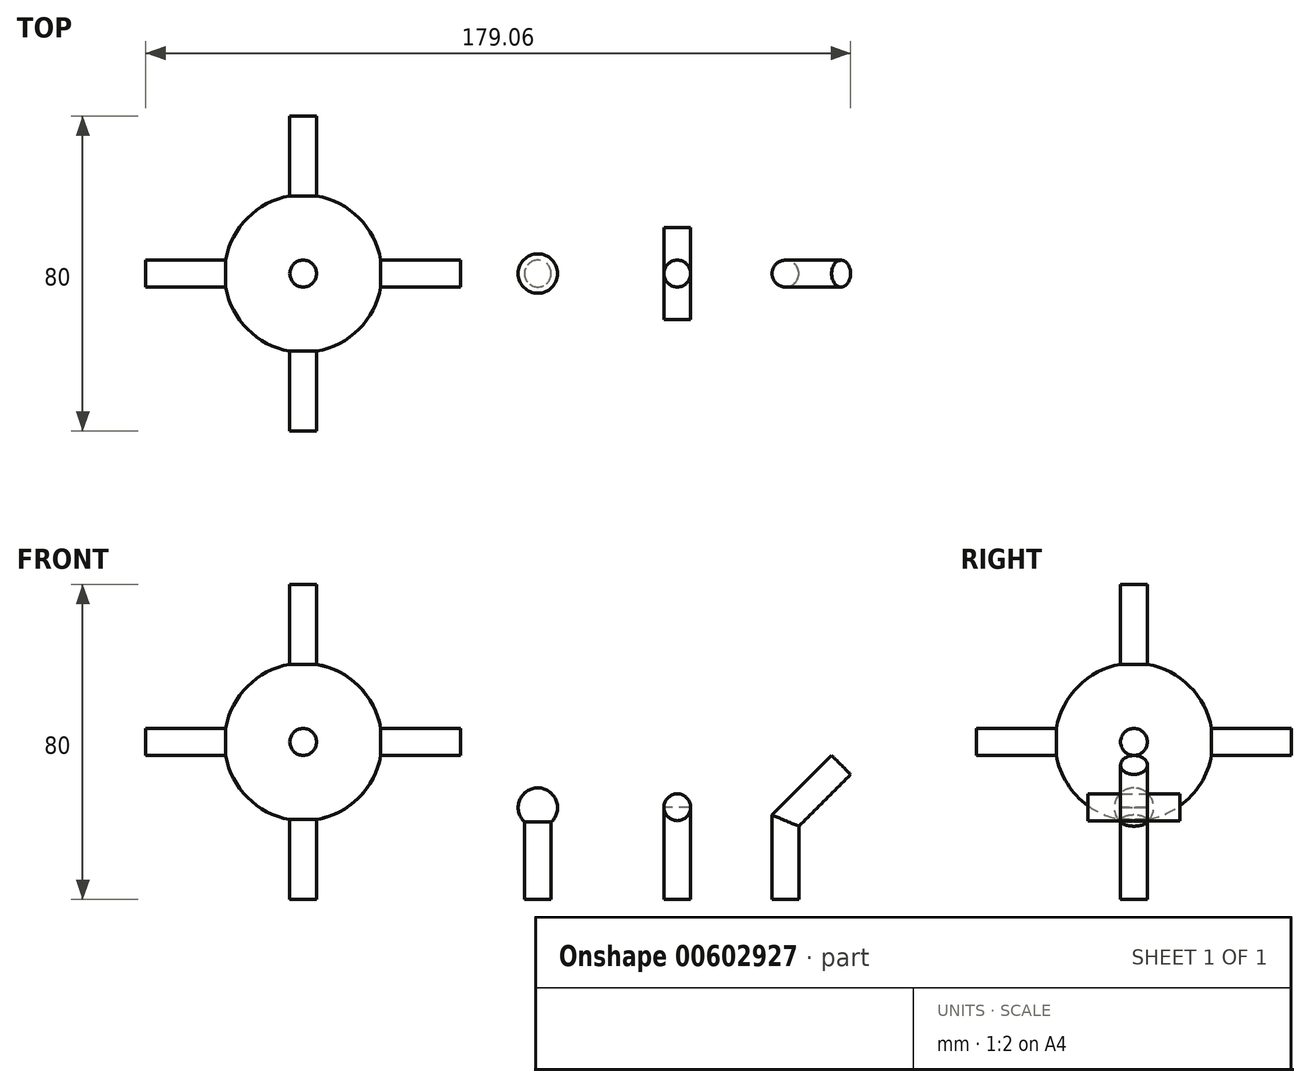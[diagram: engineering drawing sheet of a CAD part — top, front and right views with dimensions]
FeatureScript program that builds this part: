
annotation { "Feature Type Name" : "Feature", "Feature Type Description" : "" }
export const myFeature = defineFeature(function(context is Context, id is Id, definition is map)
    precondition{}
    {
        {
            var Q0;
            Q0=qCreatedBy(makeId("Top.planeOp"),FACE);
            var sketch = newSketch(context, id + "F0", { "sketchPlane" : qUnion([Q0])});
            skCircle(sketch, "E0", {"center": v(0, 0) * mm, "radius": 3.4 * mm});
            skSolve(sketch);
        }
        {
            var Q0;
            Q0 = qSketchRegion(id + "F0", true);
            extrude(context, id + "F1", {"entities" : qUnion([Q0]), "depth" : 20 * mm, "offsetDistance" : 25.4 * mm});
        }
        {
            var Q0;
            Q0=qCreatedBy(makeId("Right.planeOp"),FACE);
            var sketch = newSketch(context, id + "F2", { "sketchPlane" : qUnion([Q0])});
            skLineSegment(sketch, "E1", {"start": v(0, 18.32) * mm, "end": v(0, 28.32) * mm});
            skArc(sketch, "E2", {"start": v(0, 18.32) * mm, "mid": v(5, 23.32) * mm, "end": v(0, 28.32) * mm});
            skSolve(sketch);
        }
        {
            var Q0;
            Q0 = qSketchRegion(id + "F2", true);
            var Q1;
            Q1=makeQuery(id+"F1.opExtrude","SWEPT_FACE",FACE,{"disambiguationData":[OSD([sQuery(id+"F0.wireOp",EDGE,"E0")])]});
            revolve(context, id + "F3", {"operationType" : NewBodyOperationType.ADD, "entities" : qUnion([Q0]), "axis" : qUnion([Q1]), "revolveType" : RevolveType.FULL});
        }
        {
            var Q0;
            Q0=qCreatedBy(makeId("Top.planeOp"),FACE);
            var sketch = newSketch(context, id + "F4", { "sketchPlane" : qUnion([Q0])});
            skCircle(sketch, "E3", {"center": v(35.42, 0) * mm, "radius": 3.4 * mm});
            skSolve(sketch);
        }
        {
            var Q0;
            Q0 = qSketchRegion(id + "F4", true);
            extrude(context, id + "F5", {"entities" : qUnion([Q0]), "depth" : 23.4 * mm, "offsetDistance" : 25 * mm});
        }
        {
            var Q0;
            Q0=qCreatedBy(makeId("Front.planeOp"),FACE);
            var sketch = newSketch(context, id + "F6", { "sketchPlane" : qUnion([Q0])});
            skCircle(sketch, "E4", {"center": v(35.42, 23.4) * mm, "radius": 3.4 * mm});
            skLineSegment(sketch, "E5.0", {"start": v(32.02, 23.4) * mm, "end": v(38.82, 23.4) * mm, "construction": true});
            skSolve(sketch);
        }
        {
            var Q0;
            Q0=makeQuery(id+"F6.imprint","IMPRINT",FACE,{"disambiguationData":[TD([[makeQuery(id+"F6.imprint","IMPRINT",EDGE,{"derivedFrom":sQuery(id+"F6.wireOp",EDGE,"E4")}),1.0]])]});
            var Q1;
            Q1 = qConstructionFilter(qBodyType(qCreatedBy(id + "F6" ,EDGE), BodyType.WIRE), ConstructionObject.NO);
            extrude(context, id + "F7", {"entities" : qUnion([Q0]), "surfaceEntities" : qUnion([Q1]), "endBound" : BoundingType.SYMMETRIC, "depth" : (46.8 / 2) * mm, "offsetDistance" : 25 * mm});
        }
        {
            var Q0;
            Q0=qCreatedBy(makeId("Front.planeOp"),FACE);
            var sketch = newSketch(context, id + "F8", { "sketchPlane" : qUnion([Q0])});
            skLineSegment(sketch, "E6", {"start": v(62.9, 0) * mm, "end": v(62.9, 20) * mm});
            skLineSegment(sketch, "E7", {"start": v(62.9, 20) * mm, "end": v(77.04, 34.14) * mm});
            skSolve(sketch);
        }
        {
            var Q0;
            Q0=qCreatedBy(makeId("Top.planeOp"),FACE);
            var sketch = newSketch(context, id + "F9", { "sketchPlane" : qUnion([Q0])});
            skPoint(sketch, "E8.0", {"position": v(62.9, 0) * mm});
            skCircle(sketch, "E9", {"center": v(62.9, 0) * mm, "radius": 3.4 * mm});
            skSolve(sketch);
        }
        {
            var Q0;
            Q0=makeQuery(id+"F9.imprint","IMPRINT",FACE,{"disambiguationData":[TD([[makeQuery(id+"F9.imprint","IMPRINT",EDGE,{"derivedFrom":sQuery(id+"F9.wireOp",EDGE,"E9")}),1.0]])]});
            var Q1;
            Q1=sQuery(id+"F8.wireOp",EDGE,"E6");
            var Q2;
            Q2=sQuery(id+"F8.wireOp",EDGE,"E7");
            sweep(context, id + "F10", {"profiles" : qUnion([Q0]), "path" : qUnion([Q1, Q2])});
        }
        {
            var Q0;
            Q0=qCreatedBy(makeId("Top.planeOp"),FACE);
            var sketch = newSketch(context, id + "F11", { "sketchPlane" : qUnion([Q0])});
            skCircle(sketch, "E10", {"center": v(-59.62, 0) * mm, "radius": 3.4 * mm});
            skSolve(sketch);
        }
        {
            var Q0;
            Q0 = qSketchRegion(id + "F11", true);
            extrude(context, id + "F12", {"entities" : qUnion([Q0]), "depth" : 80 * mm, "offsetDistance" : 25 * mm});
        }
        {
            var Q0;
            Q0=qCreatedBy(makeId("Front.planeOp"),FACE);
            var sketch = newSketch(context, id + "F13", { "sketchPlane" : qUnion([Q0])});
            skLineSegment(sketch, "E11.0", {"start": v(-63.02, 0) * mm, "end": v(-56.22, 0) * mm, "construction": true});
            skCircle(sketch, "E12", {"center": v(-59.62, 40) * mm, "radius": 3.4 * mm});
            skPoint(sketch, "E12.centerSnap0", {"position": v(-59.62, 0) * mm});
            skSolve(sketch);
        }
        {
            var Q0;
            Q0 = qSketchRegion(id + "F13", true);
            extrude(context, id + "F14", {"entities" : qUnion([Q0]), "operationType" : NewBodyOperationType.ADD, "endBound" : BoundingType.SYMMETRIC, "depth" : 80 * mm, "offsetDistance" : 25 * mm});
        }
        {
            var Q0;
            Q0=sQuery(id+"F13.wireOp",EDGE,"E11.0");
            cPoint(context, id + "F15", {"entities" : qUnion([Q0]), "parameter" : 0.5});
        }
        {
            var Q0;
            Q0=qCreatedBy(makeId("Right.planeOp"),FACE);
            var Q1;
            Q1 = qCreatedBy(id + "F15" ,VERTEX);
            cPlane(context, id + "F16", {"entities" : qUnion([Q0, Q1]), "cplaneType" : CPlaneType.PLANE_POINT, "offset" : 25 * mm, "width" : 150 * mm, "height" : 150 * mm});
        }
        {
            var Q0;
            Q0=qCreatedBy(id+"F16.planeOp",FACE);
            var sketch = newSketch(context, id + "F17", { "sketchPlane" : qUnion([Q0])});
            skPoint(sketch, "E13.0", {"position": v(0, 0) * mm});
            skCircle(sketch, "E14", {"center": v(0, 40) * mm, "radius": 3.4 * mm});
            skSolve(sketch);
        }
        {
            var Q0;
            Q0 = qSketchRegion(id + "F17", true);
            extrude(context, id + "F18", {"entities" : qUnion([Q0]), "operationType" : NewBodyOperationType.ADD, "endBound" : BoundingType.SYMMETRIC, "depth" : 80 * mm, "offsetDistance" : 25 * mm});
        }
        {
            var Q0;
            Q0=qCreatedBy(makeId("Front.planeOp"),FACE);
            var sketch = newSketch(context, id + "F19", { "sketchPlane" : qUnion([Q0])});
            skPoint(sketch, "E15.0", {"position": v(-59.62, 40) * mm});
            skLineSegment(sketch, "E16", {"start": v(-59.62, 60) * mm, "end": v(-59.62, 20) * mm});
            skArc(sketch, "E17", {"start": v(-59.62, 60) * mm, "mid": v(-79.62, 40) * mm, "end": v(-59.62, 20) * mm});
            skSolve(sketch);
        }
        {
            var Q0;
            Q0 = qSketchRegion(id + "F19", true);
            var Q1;
            Q1=sQuery(id+"F19.wireOp",EDGE,"E16");
            revolve(context, id + "F20", {"operationType" : NewBodyOperationType.ADD, "entities" : qUnion([Q0]), "axis" : qUnion([Q1]), "revolveType" : RevolveType.FULL});
        }
    });
